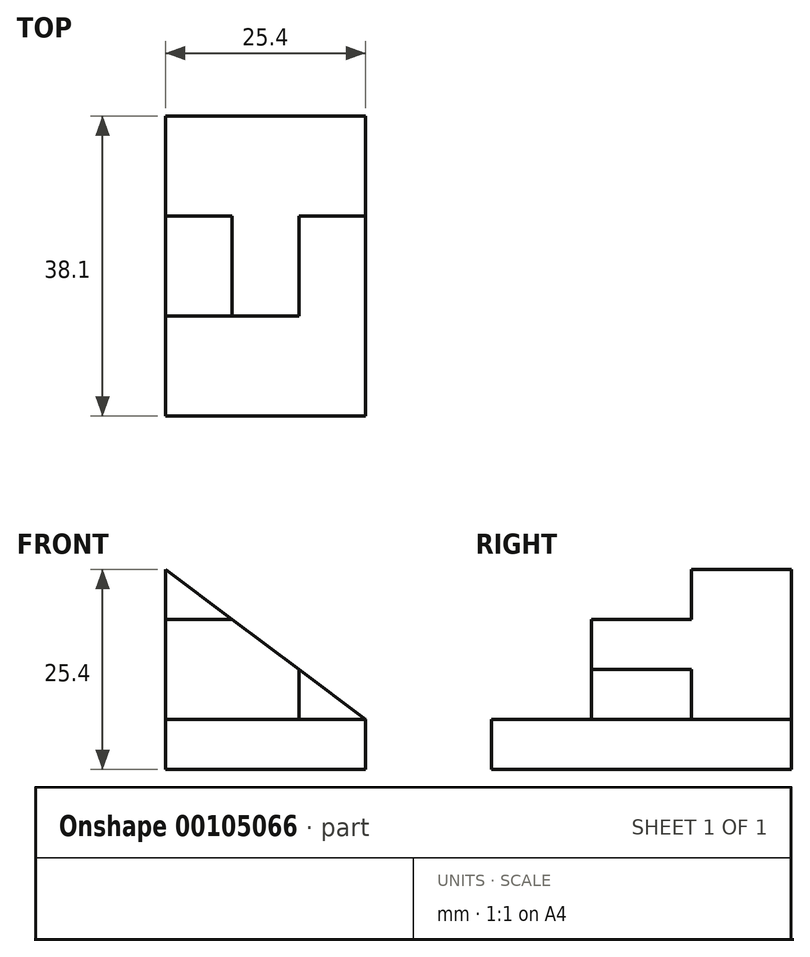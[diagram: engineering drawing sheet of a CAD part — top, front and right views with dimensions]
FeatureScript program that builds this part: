
annotation { "Feature Type Name" : "Feature", "Feature Type Description" : "" }
export const myFeature = defineFeature(function(context is Context, id is Id, definition is map)
    precondition{}
    {
        {
            var Q0;
            Q0=qCreatedBy(makeId("Front.planeOp"),FACE);
            var sketch = newSketch(context, id + "F0", { "sketchPlane" : qUnion([Q0])});
            skLineSegment(sketch, "E0.bottom", {"start": v(0, 0) * mm, "end": v(25.4, 0) * mm});
            skLineSegment(sketch, "E0.left", {"start": v(0, 0) * mm, "end": v(0, 6.35) * mm});
            skLineSegment(sketch, "E0.right", {"start": v(25.4, 0) * mm, "end": v(25.4, 6.35) * mm});
            skLineSegment(sketch, "E1.left", {"start": v(0, 6.35) * mm, "end": v(0, 25.4) * mm});
            skLineSegment(sketch, "E2", {"start": v(0, 25.4) * mm, "end": v(25.4, 6.35) * mm});
            skLineSegment(sketch, "E3", {"start": v(0, 6.35) * mm, "end": v(25.4, 6.35) * mm});
            skLineSegment(sketch, "E4", {"start": v(0, 19.05) * mm, "end": v(8.47, 19.05) * mm});
            skLineSegment(sketch, "E5", {"start": v(16.93, 12.7) * mm, "end": v(16.93, 6.35) * mm});
            skLineSegment(sketch, "E6", {"start": v(25.4, 6.35) * mm, "end": v(25.4, 25.4) * mm});
            skLineSegment(sketch, "E7", {"start": v(25.4, 25.4) * mm, "end": v(0, 25.4) * mm});
            skLineSegment(sketch, "E8", {"start": v(16.93, 12.7) * mm, "end": v(0, 12.7) * mm});
            skSolve(sketch);
        }
        {
            var Q0;
            Q0=qCreatedBy(makeId("Right.planeOp"),FACE);
            var sketch = newSketch(context, id + "F1", { "sketchPlane" : qUnion([Q0])});
            skLineSegment(sketch, "E9.bottom", {"start": v(0, 0) * mm, "end": v(-38.1, 0) * mm});
            skLineSegment(sketch, "E9.top", {"start": v(0, 6.35) * mm, "end": v(-38.1, 6.35) * mm});
            skLineSegment(sketch, "E9.left", {"start": v(0, 0) * mm, "end": v(0, 6.35) * mm});
            skLineSegment(sketch, "E9.right", {"start": v(-38.1, 0) * mm, "end": v(-38.1, 6.35) * mm});
            skLineSegment(sketch, "E10.bottom", {"start": v(-25.4, 6.35) * mm, "end": v(-12.7, 6.35) * mm});
            skLineSegment(sketch, "E10.top", {"start": v(-25.4, 12.7) * mm, "end": v(-12.7, 12.7) * mm});
            skLineSegment(sketch, "E10.left", {"start": v(-25.4, 6.35) * mm, "end": v(-25.4, 12.7) * mm});
            skLineSegment(sketch, "E10.right", {"start": v(-12.7, 6.35) * mm, "end": v(-12.7, 12.7) * mm});
            skLineSegment(sketch, "E11", {"start": v(-25.4, 12.7) * mm, "end": v(-25.4, 19.05) * mm});
            skLineSegment(sketch, "E12", {"start": v(-25.4, 19.05) * mm, "end": v(-12.7, 19.05) * mm});
            skLineSegment(sketch, "E13", {"start": v(-12.7, 19.05) * mm, "end": v(-12.7, 25.4) * mm});
            skLineSegment(sketch, "E14", {"start": v(-12.7, 25.4) * mm, "end": v(0, 25.4) * mm});
            skLineSegment(sketch, "E15", {"start": v(0, 25.4) * mm, "end": v(0, 6.35) * mm});
            skSolve(sketch);
        }
        {
            var Q0;
            Q0=makeQuery(id+"F1.imprint","IMPRINT",FACE,{"disambiguationData":[TD([[makeQuery(id+"F1.imprint","IMPRINT",EDGE,{"derivedFrom":sQuery(id+"F1.wireOp",EDGE,"E9.bottom")}),-1.0]])]});
            extrude(context, id + "F2", {"entities" : qUnion([Q0]), "depth" : 25.4 * mm});
        }
        {
            var Q0;
            Q0=makeQuery(id+"F1.imprint","IMPRINT",FACE,{"disambiguationData":[TD([[makeQuery(id+"F1.imprint","IMPRINT",EDGE,{"derivedFrom":sQuery(id+"F1.wireOp",EDGE,"E10.top")}),1.0]])]});
            extrude(context, id + "F3", {"entities" : qUnion([Q0]), "operationType" : NewBodyOperationType.ADD, "depth" : 25.4 * mm});
        }
        {
            var Q0;
            {var subQ0=sQuery(id+"F0.wireOp",EDGE,"E6");Q0=makeQuery(id+"F0.imprint","IMPRINT",FACE,{"disambiguationData":[TD([[makeQuery(id+"F0.imprint","IMPRINT",EDGE,{"derivedFrom":subQ0}),1.0]])]});}
            extrude(context, id + "F4", {"entities" : qUnion([Q0]), "operationType" : NewBodyOperationType.REMOVE, "endBound" : BoundingType.THROUGH_ALL, "depth" : 25.4 * mm});
        }
        {
            var Q0;
            {var subQ4=sQuery(id+"F0.wireOp",EDGE,"E5");Q0=makeQuery(id+"F0.imprint","IMPRINT",FACE,{"disambiguationData":[TD([[makeQuery(id+"F0.imprint","IMPRINT",EDGE,{"derivedFrom":subQ4}),-1.0]])]});}
            extrude(context, id + "F5", {"entities" : qUnion([Q0]), "operationType" : NewBodyOperationType.ADD, "depth" : 25.4 * mm});
        }
    });
